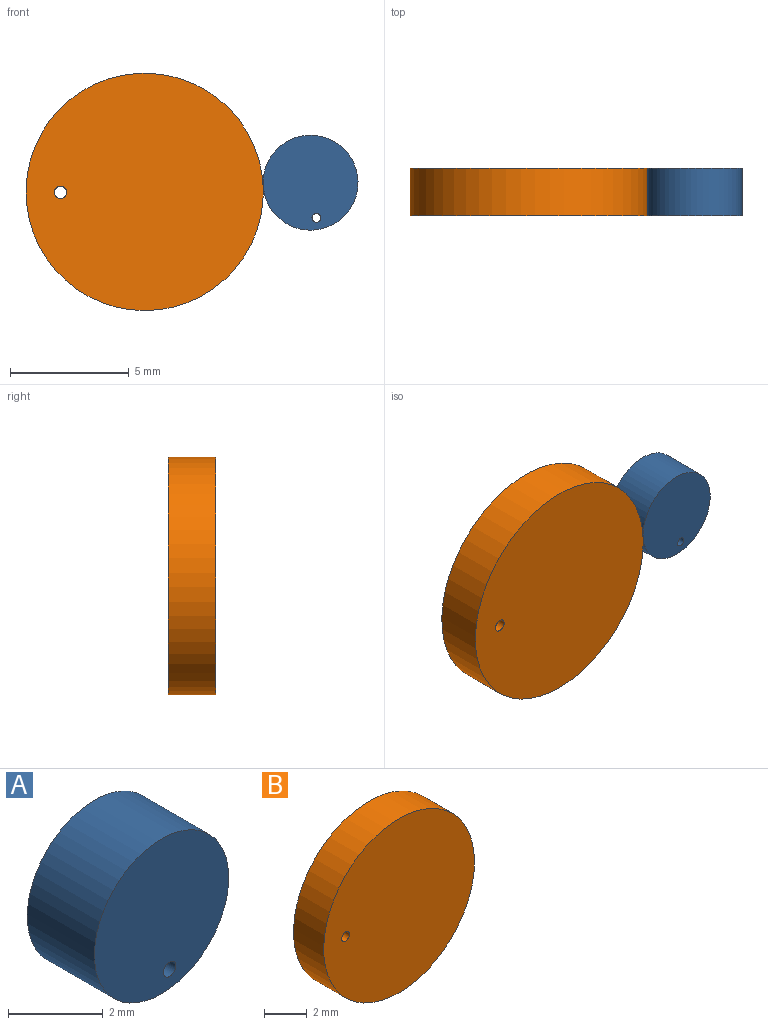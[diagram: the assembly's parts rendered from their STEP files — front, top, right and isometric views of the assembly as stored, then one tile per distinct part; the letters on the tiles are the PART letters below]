
ASSEMBLY  parts=2 mates=1
PART A: 4 faces, bbox 4x2x4 mm
  f0: cylinder r=0.19mm len=2mm, axis (0,1,0), area 2.3mm2, adj f2,f3
  f1: cylinder r=2mm len=4mm, axis (0,1,0), area 25.1mm2, adj f2,f3
  f2: plane 4x4mm, normal (0,-1,0), area 12.5mm2, adj f0,f1
  f3: plane 4x4mm, normal (0,1,0), area 12.5mm2, adj f0,f1
PART B: 4 faces, bbox 10x2x10 mm
  f0: cylinder r=0.26mm len=2mm, axis (0,1,0), area 3.2mm2, adj f2,f3
  f1: cylinder r=5mm len=10mm, axis (0,1,0), area 62.8mm2, adj f2,f3
  f2: plane 10x10mm, normal (0,-1,0), area 78.3mm2, adj f0,f1
  f3: plane 10x10mm, normal (0,1,0), area 78.3mm2, adj f0,f1
PLACE A rot(axis=(0,-1,0),0.3deg) t=(0.93,0,-3.14)mm
PLACE B rot(axis=(0,-1,0),0.3deg) t=(-0.01,0,0)mm
MATE planar A.f1 <-> B.f1  axis (0,-1,0) through (6.98,-2,0.39)mm
